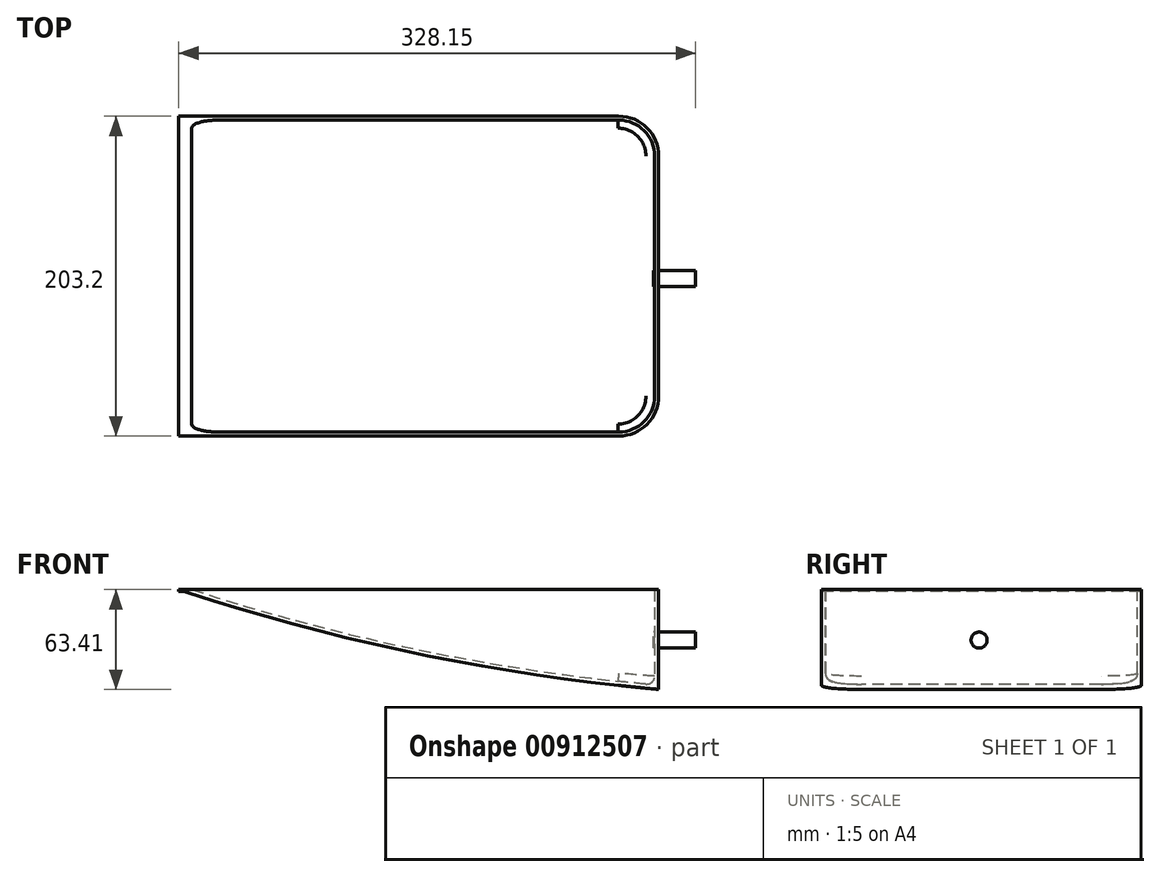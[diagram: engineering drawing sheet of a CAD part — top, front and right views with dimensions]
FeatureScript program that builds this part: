
annotation { "Feature Type Name" : "Feature", "Feature Type Description" : "" }
export const myFeature = defineFeature(function(context is Context, id is Id, definition is map)
    precondition{}
    {
        {
            var Q0;
            Q0=qCreatedBy(makeId("Top.planeOp"),FACE);
            var sketch = newSketch(context, id + "F0", { "sketchPlane" : qUnion([Q0])});
            skLineSegment(sketch, "E0.bottom", {"start": v(-163.05, 126.86) * mm, "end": v(116.35, 126.86) * mm});
            skLineSegment(sketch, "E0.top", {"start": v(-163.05, -76.34) * mm, "end": v(116.35, -76.34) * mm});
            skLineSegment(sketch, "E0.left", {"start": v(-163.05, 126.86) * mm, "end": v(-163.05, -76.34) * mm});
            skLineSegment(sketch, "E0.right", {"start": v(141.75, 101.46) * mm, "end": v(141.75, -50.94) * mm});
            skPoint(sketch, "E1.visualSharp", {"position": v(141.75, -76.34) * mm});
            skArc(sketch, "E1.filletArc", {"start": v(116.35, -76.34) * mm, "mid": v(134.3, -68.9) * mm, "end": v(141.75, -50.94) * mm});
            skPoint(sketch, "E2.visualSharp", {"position": v(141.75, 126.86) * mm});
            skArc(sketch, "E2.filletArc", {"start": v(141.75, 101.46) * mm, "mid": v(134.3, 119.42) * mm, "end": v(116.35, 126.86) * mm});
            skSolve(sketch);
        }
        {
            var Q0;
            Q0 = qSketchRegion(id + "F0", true);
            extrude(context, id + "F1", {"entities" : qUnion([Q0]), "depth" : 63.5 * mm, "offsetDistance" : 25.4 * mm});
        }
        {
            var Q0;
            Q0=makeQuery(id+"F1.opExtrude","SWEPT_FACE",FACE,{"disambiguationData":[OSD([sQuery(id+"F0.wireOp",EDGE,"E0.top")])]});
            var sketch = newSketch(context, id + "F2", { "sketchPlane" : qUnion([Q0])});
            skArc(sketch, "E3", {"start": v(-157.63, 61.71) * mm, "mid": v(-9.21, 22.32) * mm, "end": v(142.71, 0) * mm});
            skLineSegment(sketch, "E4", {"start": v(-168, 60.6) * mm, "end": v(-203.36, 39.87) * mm});
            skLineSegment(sketch, "E5", {"start": v(-203.36, 39.87) * mm, "end": v(-177, -30.4) * mm});
            skLineSegment(sketch, "E6", {"start": v(-177, -30.4) * mm, "end": v(119.4, -30.4) * mm});
            skLineSegment(sketch, "E7", {"start": v(119.4, -30.4) * mm, "end": v(142.71, 0) * mm});
            skPoint(sketch, "E8.visualSharp", {"position": v(-163.05, 63.5) * mm});
            skArc(sketch, "E8.filletArc", {"start": v(-157.63, 61.71) * mm, "mid": v(-162.94, 62.27) * mm, "end": v(-168, 60.6) * mm});
            skSolve(sketch);
        }
        {
            var Q0;
            Q0=makeQuery(id+"F2.imprint","IMPRINT",FACE,{"disambiguationData":[TD([[makeQuery(id+"F2.imprint","IMPRINT",EDGE,{"derivedFrom":sQuery(id+"F2.wireOp",EDGE,"E4")}),1.0]])]});
            var Q1;
            {var subQ1=sQuery(id+"F0.wireOp",EDGE,"E0.top");var subQ5=makeQuery(id+"F1.opExtrude","CAP_EDGE",EDGE,{"disambiguationData":[OSD([subQ1])],"isStart":true});Q1=makeQuery(id+"F2.imprint","IMPRINT",FACE,{"disambiguationData":[TD([[makeQuery(id+"F2.imprint","IMPRINT",EDGE,{"derivedFrom":subQ5}),1.0]])]});}
            extrude(context, id + "F3", {"entities" : qUnion([Q0, Q1]), "operationType" : NewBodyOperationType.REMOVE, "oppositeDirection" : true, "depth" : 336.8 * mm, "offsetDistance" : 25.4 * mm});
        }
        {
            var Q0;
            Q0=makeQuery(id+"F1.opExtrude","CAP_FACE",FACE,{"disambiguationData":[OSD([sQuery(id+"F0.wireOp",EDGE,"E0.bottom"),sQuery(id+"F0.wireOp",EDGE,"E0.top"),sQuery(id+"F0.wireOp",EDGE,"E0.left"),sQuery(id+"F0.wireOp",EDGE,"E0.right")])],"isStart":false});
            var Q1;
            Q1=makeQuery(id+"F1.opExtrude","SWEPT_FACE",FACE,{"disambiguationData":[OSD([sQuery(id+"F0.wireOp",EDGE,"E0.left")])]});
            shell(context, id + "F4", {"entities" : qUnion([Q0, Q1]), "thickness" : 2.54 * mm});
        }
        {
            var Q0;
            Q0=qCreatedBy(makeId("Right.planeOp"),FACE);
            var sketch = newSketch(context, id + "F5", { "sketchPlane" : qUnion([Q0])});
            skCircle(sketch, "E9", {"center": v(23.76, 31.4) * mm, "radius": 5.08 * mm});
            skSolve(sketch);
        }
        {
            var Q0;
            Q0 = qSketchRegion(id + "F5", true);
            extrude(context, id + "F6", {"entities" : qUnion([Q0]), "operationType" : NewBodyOperationType.ADD, "depth" : 165.1 * mm, "offsetDistance" : 25.4 * mm, "hasSecondDirection" : true, "secondDirectionOppositeDirection" : false, "secondDirectionDepth" : 138.43 * mm});
        }
        {
            var Q0;
            Q0=makeQuery(id+"F4.opShell","OFFSET_EDGE",EDGE,{"disambiguationData":[OSD([sQuery(id+"F0.wireOp",EDGE,"E0.bottom"),sQuery(id+"F2.wireOp",EDGE,"E3")])]});
            fillet(context, id + "F7", {"entities" : qUnion([Q0]), "radius" : 5.08 * mm, "tangentPropagation" : true, "allowEdgeOverflow" : false});
        }
    });
